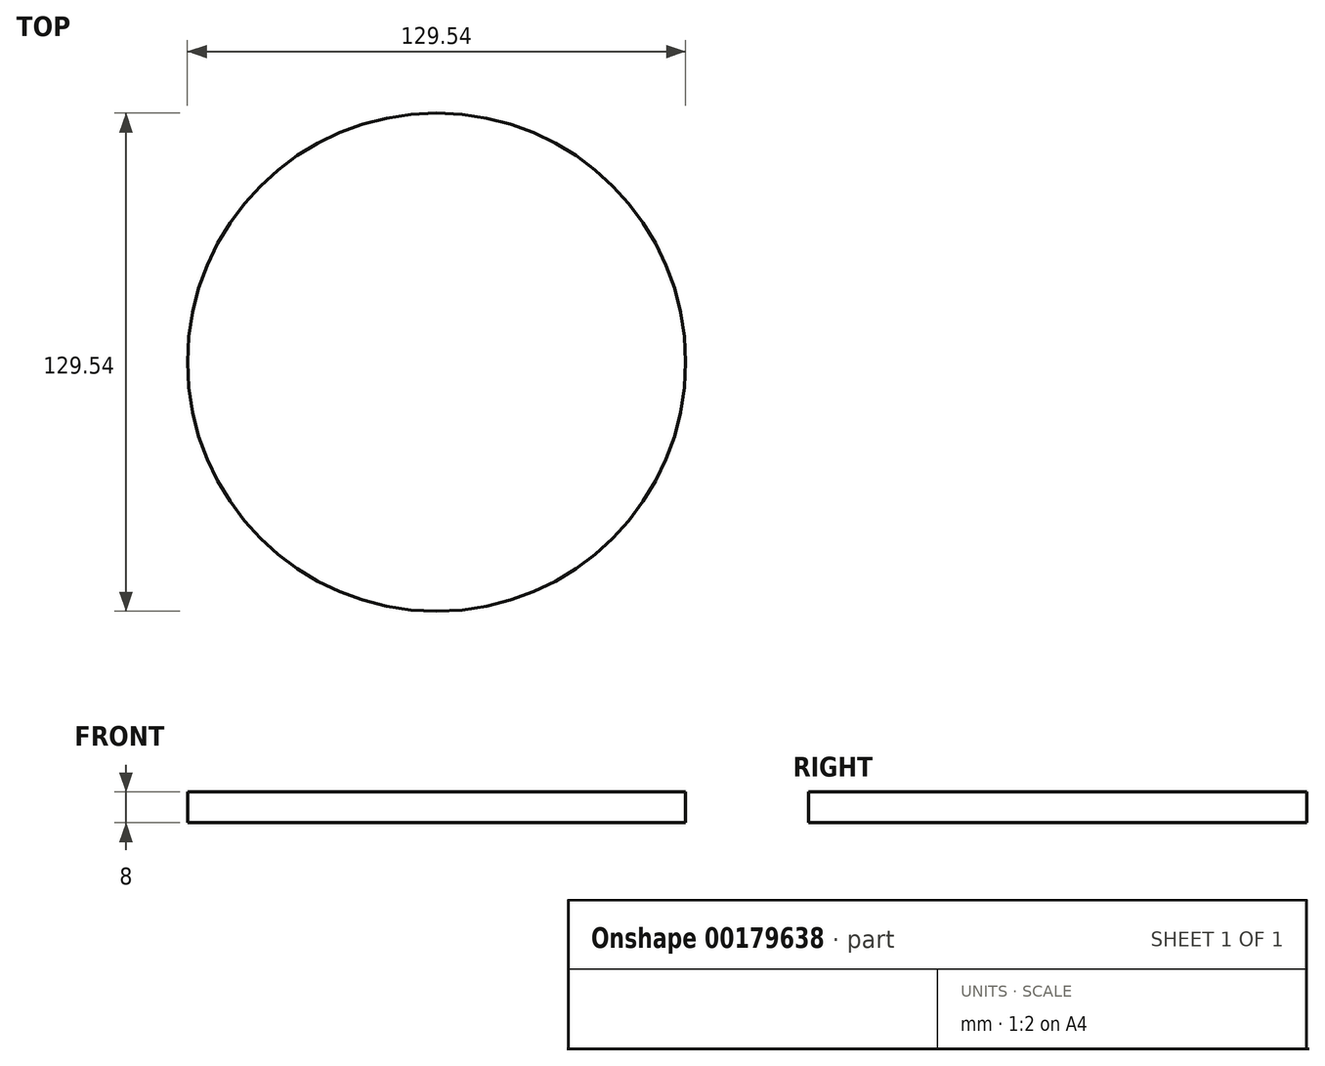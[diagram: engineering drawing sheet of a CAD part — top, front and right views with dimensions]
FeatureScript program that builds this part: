
annotation { "Feature Type Name" : "Feature", "Feature Type Description" : "" }
export const myFeature = defineFeature(function(context is Context, id is Id, definition is map)
    precondition{}
    {
        {
            var Q0;
            Q0=qCreatedBy(makeId("Top.planeOp"),FACE);
            var sketch = newSketch(context, id + "F0", { "sketchPlane" : qUnion([Q0])});
            skCircle(sketch, "E0", {"center": v(0, 0) * mm, "radius": 64.77 * mm});
            skSolve(sketch);
        }
        {
            var Q0;
            Q0 = qSketchRegion(id + "F0", true);
            extrude(context, id + "F1", {"entities" : qUnion([Q0]), "depth" : 8 * mm});
        }
        {
            var Q0;
            Q0=makeQuery(id+"F1.opExtrude","CAP_FACE",FACE,{"disambiguationData":[OSD([sQuery(id+"F0.wireOp",EDGE,"E0")])],"isStart":false});
            var sketch = newSketch(context, id + "F2", { "sketchPlane" : qUnion([Q0])});
            skSolve(sketch);
        }
        {
            var Q0;
            Q0=makeQuery(id+"F2.imprint","IMPRINT",FACE,{"disambiguationData":[TD([[makeQuery(id+"F2.imprint","IMPRINT",EDGE,{"derivedFrom":makeQuery(id+"F1.opExtrude","CAP_EDGE",EDGE,{"disambiguationData":[OSD([sQuery(id+"F0.wireOp",EDGE,"E0")])],"isStart":false})}),1.0]])]});
            var sketch = newSketch(context, id + "F3", { "sketchPlane" : qUnion([Q0])});
            skCircle(sketch, "E1", {"center": v(0, 0) * mm, "radius": 60.43 * mm});
            skSolve(sketch);
        }
        {
            var Q0;
            Q0=makeQuery(id+"F3.imprint","IMPRINT",FACE,{"disambiguationData":[TD([[makeQuery(id+"F3.imprint","IMPRINT",EDGE,{"derivedFrom":sQuery(id+"F3.wireOp",EDGE,"E1")}),1.0]])]});
            extrude(context, id + "F4", {"entities" : qUnion([Q0]), "operationType" : NewBodyOperationType.ADD, "oppositeDirection" : true, "depth" : 4 * mm});
        }
    });
